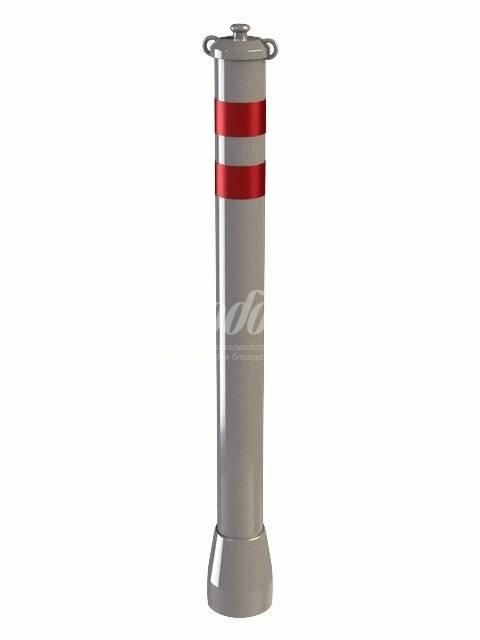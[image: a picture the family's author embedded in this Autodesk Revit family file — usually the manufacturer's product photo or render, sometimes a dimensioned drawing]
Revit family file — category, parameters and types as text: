
# Revit family: 6893 Столбик парковочный ст-2 с кольцом Хоббика
name_source: partatom
category: Антураж
revit_build: Autodesk Revit 2018 (Build: 20180423_1000(x64)
units: mm (PartAtom-declared; Revit-internal decimal feet)

## family parameters
Всегда вертикально = Да
Источник визуального образа = Геометрия семейства
На основе рабочей плоскости = Нет
Общий = Нет
При загрузке вырезать с полостями = Нет
Точка расчета площади = Нет

## types (2) — shared parameters
URL = https://hobbyka.ru
Артикул товара = Арт. 6893
Высота = 760 мм
Группа модели = Тротуарные столбики и ограждения
Диаметр = 90 мм
Длина = 90 мм
Изготовитель = ООО «Хоббика»
Изображение типоразмера = Столбик парковочный ст-2 с кольцом Арт 6893.jpg
Материал изделия = Сталь
Цвет каркаса = Сталь
Цвет отделки = Красный
Ширина = 90 мм

## per-type parameters (varying)
| type | Описание | Под анкер | Съемный |
| Под анкер | Столбик парковочный ст-2 с кольцом. Под анкер | Да | Нет |
| Съемный | Столбик парковочный ст-2 с кольцом. Съемный | Нет | Да |
